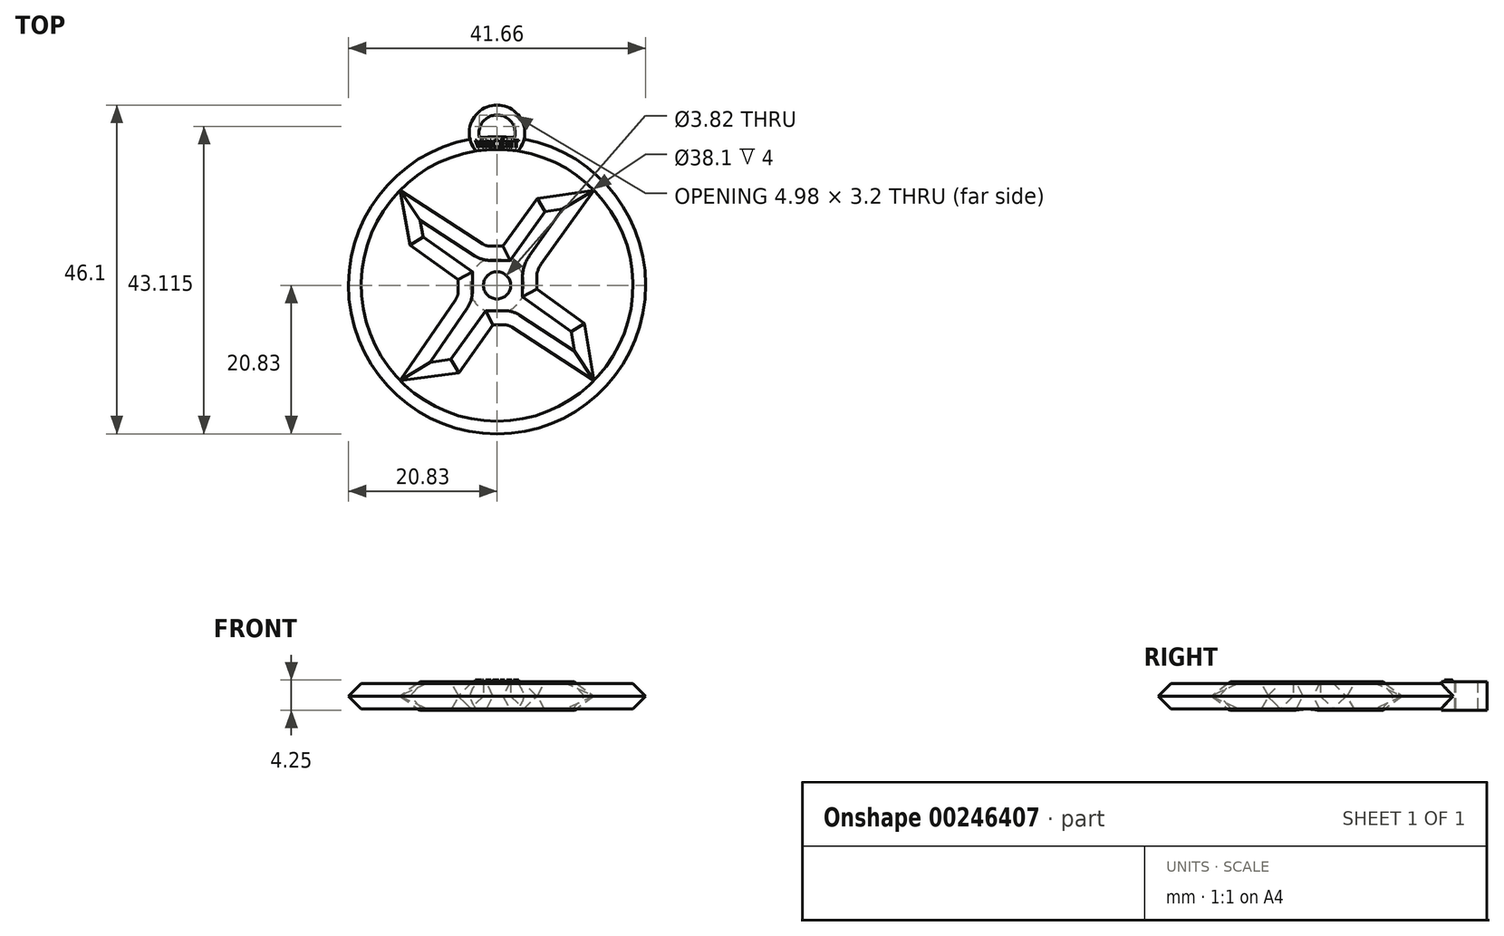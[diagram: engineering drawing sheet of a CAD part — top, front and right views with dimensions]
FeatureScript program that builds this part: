
annotation { "Feature Type Name" : "Feature", "Feature Type Description" : "" }
export const myFeature = defineFeature(function(context is Context, id is Id, definition is map)
    precondition{}
    {
        {
            var Q0;
            Q0=qCreatedBy(makeId("Top.planeOp"),FACE);
            var sketch = newSketch(context, id + "F0", { "sketchPlane" : qUnion([Q0])});
            skLineSegment(sketch, "E0.bottom", {"start": v(0.83, 5.49) * mm, "end": v(-0.91, 5.49) * mm});
            skLineSegment(sketch, "E0.top", {"start": v(1.05, -5.55) * mm, "end": v(-0.56, -5.55) * mm});
            skLineSegment(sketch, "E0.left", {"start": v(5.55, 1.05) * mm, "end": v(5.55, -0.56) * mm});
            skLineSegment(sketch, "E0.right", {"start": v(-5.46, 0.83) * mm, "end": v(-5.46, -0.92) * mm});
            skPoint(sketch, "E0.middle", {"position": v(0, 0) * mm});
            skLineSegment(sketch, "E1", {"start": v(0.83, 5.49) * mm, "end": v(5.62, 12.19) * mm});
            skLineSegment(sketch, "E2", {"start": v(5.62, 12.19) * mm, "end": v(13.6, 13.35) * mm});
            skCircle(sketch, "E3", {"center": v(0, 0) * mm, "radius": 1.91 * mm});
            skLineSegment(sketch, "E4", {"start": v(6.16, 2.95) * mm, "end": v(13.6, 13.35) * mm});
            skLineSegment(sketch, "E5", {"start": v(2.1, -5.86) * mm, "end": v(13.6, -13.35) * mm});
            skLineSegment(sketch, "E6", {"start": v(-5.8, -2) * mm, "end": v(-13.6, -13.35) * mm});
            skLineSegment(sketch, "E7", {"start": v(-2.03, 5.82) * mm, "end": v(-13.6, 13.35) * mm});
            skLineSegment(sketch, "E8", {"start": v(5.55, -0.56) * mm, "end": v(12.27, -5.35) * mm});
            skLineSegment(sketch, "E9", {"start": v(12.27, -5.35) * mm, "end": v(13.6, -13.35) * mm});
            skLineSegment(sketch, "E10", {"start": v(-0.56, -5.55) * mm, "end": v(-5.35, -12.27) * mm});
            skLineSegment(sketch, "E11", {"start": v(-5.35, -12.27) * mm, "end": v(-13.6, -13.35) * mm});
            skLineSegment(sketch, "E12", {"start": v(-5.46, 0.83) * mm, "end": v(-12.18, 5.63) * mm});
            skLineSegment(sketch, "E13", {"start": v(-12.18, 5.63) * mm, "end": v(-13.6, 13.35) * mm});
            skPoint(sketch, "E14.start.orphan", {"position": v(1.91, 0) * mm});
            skPoint(sketch, "E15.start.orphan", {"position": v(0, -1.91) * mm});
            skPoint(sketch, "E16.start.orphan", {"position": v(-1.91, 0) * mm});
            skPoint(sketch, "E17.start.orphan", {"position": v(0, 1.91) * mm});
            skPoint(sketch, "E18.visualSharp", {"position": v(-1.52, 5.49) * mm});
            skArc(sketch, "E18.filletArc", {"start": v(-2.03, 5.82) * mm, "mid": v(-1.5, 5.57) * mm, "end": v(-0.91, 5.49) * mm});
            skPoint(sketch, "E19.visualSharp", {"position": v(-5.46, -1.52) * mm});
            skArc(sketch, "E19.filletArc", {"start": v(-5.8, -2) * mm, "mid": v(-5.55, -1.5) * mm, "end": v(-5.46, -0.92) * mm});
            skPoint(sketch, "E20.visualSharp", {"position": v(5.55, 2.1) * mm});
            skArc(sketch, "E20.filletArc", {"start": v(6.16, 2.95) * mm, "mid": v(5.7, 2.05) * mm, "end": v(5.55, 1.05) * mm});
            skPoint(sketch, "E21.visualSharp", {"position": v(1.62, -5.55) * mm});
            skArc(sketch, "E21.filletArc", {"start": v(2.1, -5.86) * mm, "mid": v(1.6, -5.63) * mm, "end": v(1.05, -5.55) * mm});
            skLineSegment(sketch, "E22.bottom", {"start": v(-25.4, 25.4) * mm, "end": v(25.4, 25.4) * mm});
            skLineSegment(sketch, "E22.top", {"start": v(-25.4, -25.4) * mm, "end": v(25.4, -25.4) * mm});
            skLineSegment(sketch, "E22.left", {"start": v(-25.4, 25.4) * mm, "end": v(-25.4, -25.4) * mm});
            skLineSegment(sketch, "E22.right", {"start": v(25.4, 25.4) * mm, "end": v(25.4, -25.4) * mm});
            skCircle(sketch, "E23", {"center": v(0, 0) * mm, "radius": 19.05 * mm});
            skCircle(sketch, "E24", {"center": v(0, 0) * mm, "radius": 20.83 * mm});
            skArc(sketch, "E25", {"start": v(3.78, 20.48) * mm, "mid": v(0, 25.27) * mm, "end": v(-3.78, 20.48) * mm});
            skArc(sketch, "E26", {"start": v(2.45, 20.68) * mm, "mid": v(0, 23.89) * mm, "end": v(-2.45, 20.68) * mm});
            skSolve(sketch);
        }
        {
            var Q0;
            Q0=makeQuery(id+"F0.imprint","IMPRINT",FACE,{"disambiguationData":[TD([[makeQuery(id+"F0.imprint","IMPRINT",EDGE,{"derivedFrom":sQuery(id+"F0.wireOp",EDGE,"E0.bottom")}),1.0]])]});
            var Q1;
            {var subQ0=sQuery(id+"F0.wireOp",EDGE,"E25");Q1=makeQuery(id+"F0.imprint","IMPRINT",FACE,{"disambiguationData":[TD([[makeQuery(id+"F0.imprint","IMPRINT",EDGE,{"derivedFrom":subQ0}),1.0]])]});}
            var Q2;
            {var subQ3=sQuery(id+"F0.wireOp",EDGE,"E25");var subQ4=sQuery(id+"F0.wireOp",EDGE,"E24");var subQ5=makeQuery(id+"F0.imprint","INTERSECT",VERTEX,{"disambiguationData":[OD(0.0)],"derivedFrom":[subQ4,subQ3]});Q2=makeQuery(id+"F0.imprint","IMPRINT",FACE,{"disambiguationData":[TD([[makeQuery(id+"F0.imprint","IMPRINT",EDGE,{"disambiguationData":[TD([[subQ5,-1.0]])],"derivedFrom":subQ4}),1.0]])]});}
            extrude(context, id + "F1", {"entities" : qUnion([Q0, Q1, Q2]), "depth" : 4 * mm});
        }
        {
            var Q0;
            Q0=makeQuery(id+"F1.opExtrude","CAP_EDGE",EDGE,{"disambiguationData":[OSD([sQuery(id+"F0.wireOp",EDGE,"E10")])],"isStart":false});
            var Q1;
            Q1=makeQuery(id+"F1.opExtrude","CAP_EDGE",EDGE,{"disambiguationData":[OSD([sQuery(id+"F0.wireOp",EDGE,"E0.top")])],"isStart":false});
            var Q2;
            Q2=makeQuery(id+"F1.opExtrude","CAP_EDGE",EDGE,{"disambiguationData":[OSD([sQuery(id+"F0.wireOp",EDGE,"E9")])],"isStart":false});
            var Q3;
            Q3=makeQuery(id+"F1.opExtrude","CAP_EDGE",EDGE,{"disambiguationData":[OSD([sQuery(id+"F0.wireOp",EDGE,"E8")])],"isStart":false});
            var Q4;
            Q4=makeQuery(id+"F1.opExtrude","CAP_EDGE",EDGE,{"disambiguationData":[OSD([sQuery(id+"F0.wireOp",EDGE,"E4")])],"isStart":false});
            var Q5;
            Q5=makeQuery(id+"F1.opExtrude","CAP_EDGE",EDGE,{"disambiguationData":[OSD([sQuery(id+"F0.wireOp",EDGE,"E11")])],"isStart":false});
            var Q6;
            Q6=makeQuery(id+"F1.opExtrude","CAP_EDGE",EDGE,{"disambiguationData":[OSD([sQuery(id+"F0.wireOp",EDGE,"E6")])],"isStart":false});
            var Q7;
            Q7=makeQuery(id+"F1.opExtrude","CAP_EDGE",EDGE,{"disambiguationData":[OSD([sQuery(id+"F0.wireOp",EDGE,"E12")])],"isStart":false});
            var Q8;
            Q8=makeQuery(id+"F1.opExtrude","CAP_EDGE",EDGE,{"disambiguationData":[OSD([sQuery(id+"F0.wireOp",EDGE,"E13")])],"isStart":false});
            var Q9;
            Q9=makeQuery(id+"F1.opExtrude","CAP_EDGE",EDGE,{"disambiguationData":[OSD([sQuery(id+"F0.wireOp",EDGE,"E7")])],"isStart":false});
            var Q10;
            Q10=makeQuery(id+"F1.opExtrude","CAP_EDGE",EDGE,{"disambiguationData":[OSD([sQuery(id+"F0.wireOp",EDGE,"E5")])],"isStart":false});
            var Q11;
            Q11=makeQuery(id+"F1.opExtrude","CAP_EDGE",EDGE,{"disambiguationData":[OSD([sQuery(id+"F0.wireOp",EDGE,"E21.filletArc")])],"isStart":false});
            var Q12;
            Q12=makeQuery(id+"F1.opExtrude","CAP_EDGE",EDGE,{"disambiguationData":[OSD([sQuery(id+"F0.wireOp",EDGE,"E0.bottom")])],"isStart":false});
            var Q13;
            Q13=makeQuery(id+"F1.opExtrude","CAP_EDGE",EDGE,{"disambiguationData":[OSD([sQuery(id+"F0.wireOp",EDGE,"E18.filletArc")])],"isStart":false});
            var Q14;
            Q14=makeQuery(id+"F1.opExtrude","CAP_EDGE",EDGE,{"disambiguationData":[OSD([sQuery(id+"F0.wireOp",EDGE,"E1")])],"isStart":false});
            var Q15;
            Q15=makeQuery(id+"F1.opExtrude","CAP_EDGE",EDGE,{"disambiguationData":[OSD([sQuery(id+"F0.wireOp",EDGE,"E2")])],"isStart":false});
            var Q16;
            Q16=makeQuery(id+"F1.opExtrude","CAP_EDGE",EDGE,{"disambiguationData":[OSD([sQuery(id+"F0.wireOp",EDGE,"E5")])],"isStart":true});
            var Q17;
            Q17=makeQuery(id+"F1.opExtrude","CAP_EDGE",EDGE,{"disambiguationData":[OSD([sQuery(id+"F0.wireOp",EDGE,"E9")])],"isStart":true});
            var Q18;
            Q18=makeQuery(id+"F1.opExtrude","CAP_EDGE",EDGE,{"disambiguationData":[OSD([sQuery(id+"F0.wireOp",EDGE,"E8")])],"isStart":true});
            var Q19;
            Q19=makeQuery(id+"F1.opExtrude","CAP_EDGE",EDGE,{"disambiguationData":[OSD([sQuery(id+"F0.wireOp",EDGE,"E0.left")])],"isStart":true});
            var Q20;
            Q20=makeQuery(id+"F1.opExtrude","CAP_EDGE",EDGE,{"disambiguationData":[OSD([sQuery(id+"F0.wireOp",EDGE,"E4")])],"isStart":true});
            var Q21;
            Q21=makeQuery(id+"F1.opExtrude","CAP_EDGE",EDGE,{"disambiguationData":[OSD([sQuery(id+"F0.wireOp",EDGE,"E20.filletArc")])],"isStart":true});
            var Q22;
            Q22=makeQuery(id+"F1.opExtrude","CAP_EDGE",EDGE,{"disambiguationData":[OSD([sQuery(id+"F0.wireOp",EDGE,"E1")])],"isStart":true});
            var Q23;
            Q23=makeQuery(id+"F1.opExtrude","CAP_EDGE",EDGE,{"disambiguationData":[OSD([sQuery(id+"F0.wireOp",EDGE,"E2")])],"isStart":true});
            var Q24;
            Q24=makeQuery(id+"F1.opExtrude","CAP_EDGE",EDGE,{"disambiguationData":[OSD([sQuery(id+"F0.wireOp",EDGE,"E0.bottom")])],"isStart":true});
            var Q25;
            Q25=makeQuery(id+"F1.opExtrude","CAP_FACE",FACE,{"disambiguationData":[OSD([sQuery(id+"F0.wireOp",EDGE,"E0.bottom"),sQuery(id+"F0.wireOp",EDGE,"E0.top"),sQuery(id+"F0.wireOp",EDGE,"E0.left"),sQuery(id+"F0.wireOp",EDGE,"E0.right"),sQuery(id+"F0.wireOp",EDGE,"E1"),sQuery(id+"F0.wireOp",EDGE,"E2"),sQuery(id+"F0.wireOp",EDGE,"E3"),sQuery(id+"F0.wireOp",EDGE,"E4"),sQuery(id+"F0.wireOp",EDGE,"E5"),sQuery(id+"F0.wireOp",EDGE,"E6"),sQuery(id+"F0.wireOp",EDGE,"E7"),sQuery(id+"F0.wireOp",EDGE,"E8"),sQuery(id+"F0.wireOp",EDGE,"E9"),sQuery(id+"F0.wireOp",EDGE,"E10"),sQuery(id+"F0.wireOp",EDGE,"E11"),sQuery(id+"F0.wireOp",EDGE,"E12"),sQuery(id+"F0.wireOp",EDGE,"E13"),sQuery(id+"F0.wireOp",EDGE,"E18.filletArc"),sQuery(id+"F0.wireOp",EDGE,"E19.filletArc"),sQuery(id+"F0.wireOp",EDGE,"E20.filletArc"),sQuery(id+"F0.wireOp",EDGE,"E21.filletArc")])],"isStart":true});
            var Q26;
            {var subQ0=sQuery(id+"F0.wireOp",EDGE,"E25");var subQ1=sQuery(id+"F0.wireOp",EDGE,"E24");Q26=makeQuery(id+"F1.opExtrude","CAP_EDGE",EDGE,{"disambiguationData":[OSD([subQ1]),TDD([makeQuery(id+"F0.imprint","IMPRINT",EDGE,{"disambiguationData":[TD([[makeQuery(id+"F0.imprint","INTERSECT",VERTEX,{"disambiguationData":[OD(0.0)],"derivedFrom":[subQ1,subQ0]}),1.0]])],"derivedFrom":subQ1})])],"isStart":false});}
            var Q27;
            {var subQ0=sQuery(id+"F0.wireOp",EDGE,"E25");var subQ1=sQuery(id+"F0.wireOp",EDGE,"E24");Q27=makeQuery(id+"F1.opExtrude","CAP_EDGE",EDGE,{"disambiguationData":[OSD([subQ1]),TDD([makeQuery(id+"F0.imprint","IMPRINT",EDGE,{"disambiguationData":[TD([[makeQuery(id+"F0.imprint","INTERSECT",VERTEX,{"disambiguationData":[OD(0.0)],"derivedFrom":[subQ1,subQ0]}),1.0]])],"derivedFrom":subQ1})])],"isStart":true});}
            chamfer(context, id + "F2", {"entities" : qUnion([Q0, Q1, Q2, Q3, Q4, Q5, Q6, Q7, Q8, Q9, Q10, Q11, Q12, Q13, Q14, Q15, Q16, Q17, Q18, Q19, Q20, Q21, Q22, Q23, Q24, Q25, Q26, Q27]), "width" : 2 * mm, "tangentPropagation" : true});
        }
        {
            var Q0;
            Q0=makeQuery(id+"F1.opExtrude","CAP_FACE",FACE,{"disambiguationData":[OSD([sQuery(id+"F0.wireOp",EDGE,"E23"),sQuery(id+"F0.wireOp",EDGE,"E24"),sQuery(id+"F0.wireOp",EDGE,"E25"),sQuery(id+"F0.wireOp",EDGE,"E26")])],"isStart":false});
            var sketch = newSketch(context, id + "F3", { "sketchPlane" : qUnion([Q0])});
            skText(sketch, "E27", { "text": "VINCENT", "fontName": "NotoSansCJKjp-Regular.otf"});
            const initialGuessF3  = {"E27": [-0.00303, 0.01929, 1, 0, 0.00107]};
            skSetInitialGuess(sketch, initialGuessF3);
            skSolve(sketch);
        }
        {
            var Q0;
            Q0 = qSketchRegion(id + "F3", true);
            extrude(context, id + "F4", {"entities" : qUnion([Q0]), "operationType" : NewBodyOperationType.ADD, "depth" : .25 * mm});
        }
    });
